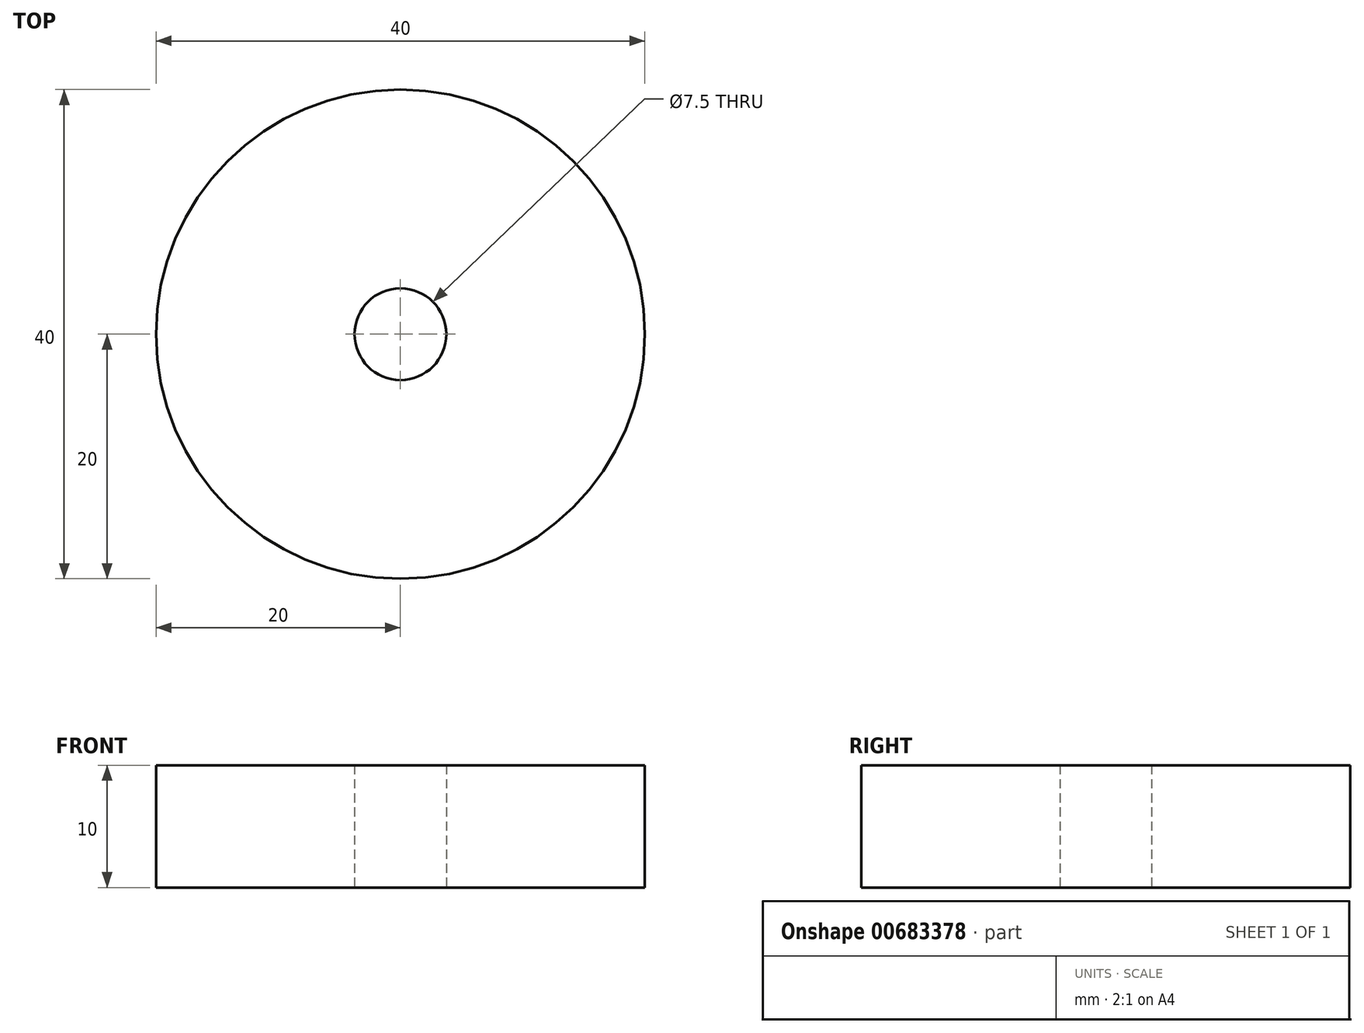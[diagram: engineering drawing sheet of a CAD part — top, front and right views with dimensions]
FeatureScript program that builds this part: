
annotation { "Feature Type Name" : "Feature", "Feature Type Description" : "" }
export const myFeature = defineFeature(function(context is Context, id is Id, definition is map)
    precondition{}
    {
        {
            var Q0;
            Q0=qCreatedBy(makeId("Top.planeOp"),FACE);
            var sketch = newSketch(context, id + "F0", { "sketchPlane" : qUnion([Q0])});
            skCircle(sketch, "E0", {"center": v(0, 0) * mm, "radius": 20 * mm});
            skCircle(sketch, "E1", {"center": v(0, 0) * mm, "radius": 3.75 * mm});
            skSolve(sketch);
        }
        {
            var Q0;
            Q0=makeQuery(id+"F0.imprint","IMPRINT",FACE,{"disambiguationData":[TD([[makeQuery(id+"F0.imprint","IMPRINT",EDGE,{"derivedFrom":sQuery(id+"F0.wireOp",EDGE,"E0")}),1.0]])]});
            extrude(context, id + "F1", {"entities" : qUnion([Q0]), "depth" : 10 * mm, "offsetDistance" : 25 * mm});
        }
    });
